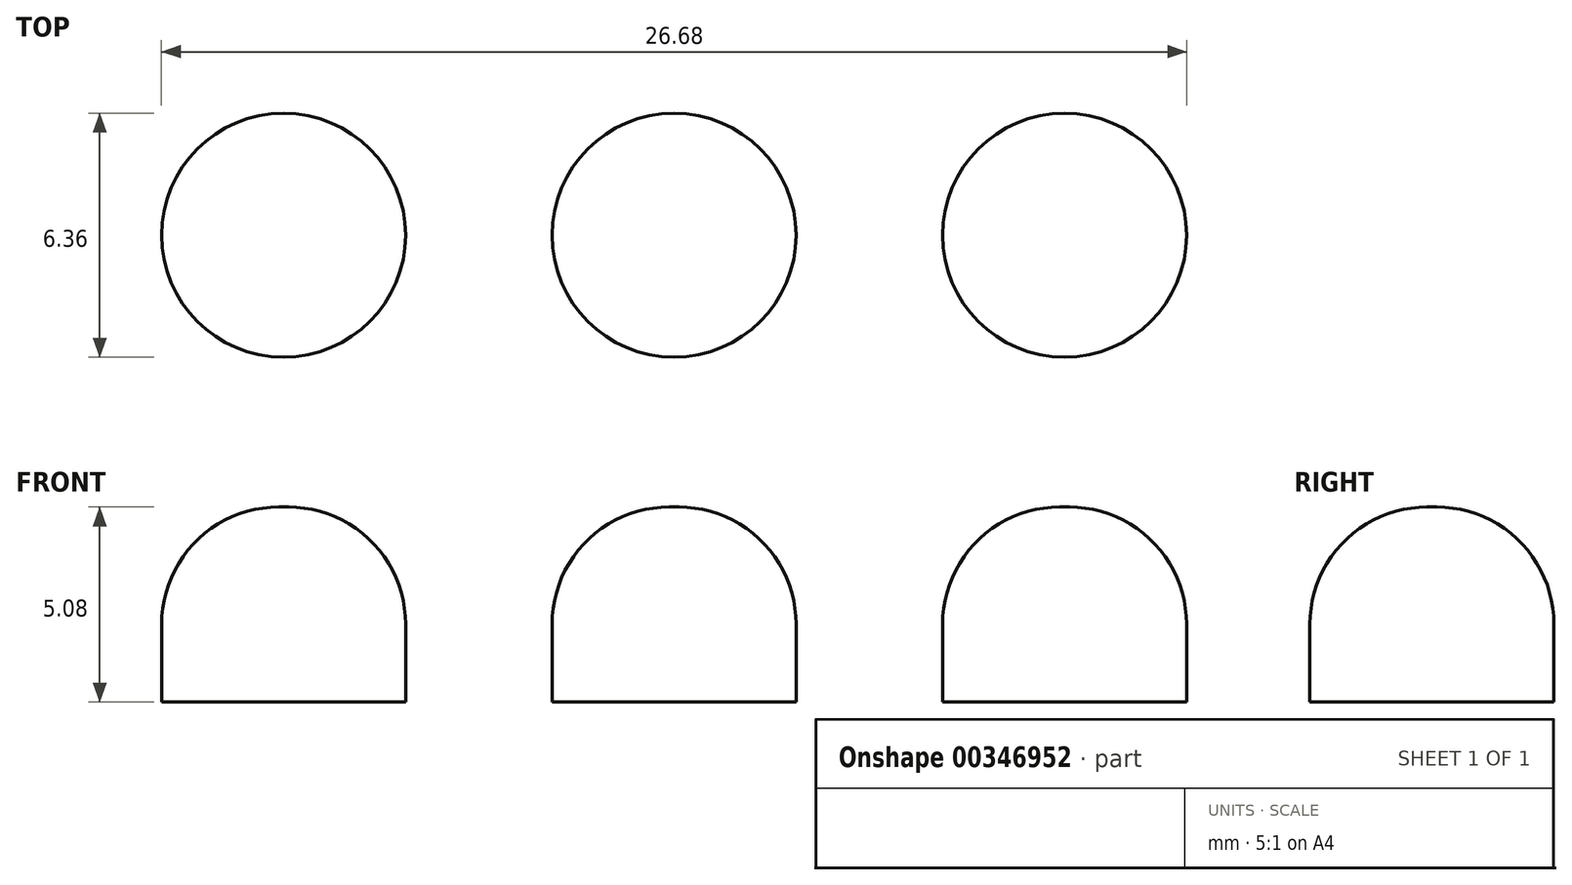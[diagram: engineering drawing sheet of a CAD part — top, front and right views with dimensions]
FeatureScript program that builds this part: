
annotation { "Feature Type Name" : "Feature", "Feature Type Description" : "" }
export const myFeature = defineFeature(function(context is Context, id is Id, definition is map)
    precondition{}
    {
        {
            var Q0;
            Q0=qCreatedBy(makeId("Top.planeOp"),FACE);
            var sketch = newSketch(context, id + "F0", { "sketchPlane" : qUnion([Q0])});
            skCircle(sketch, "E0", {"center": v(-10.16, 0) * mm, "radius": 3.18 * mm});
            skSolve(sketch);
        }
        {
            var Q0;
            Q0=qCreatedBy(makeId("Top.planeOp"),FACE);
            var sketch = newSketch(context, id + "F1", { "sketchPlane" : qUnion([Q0])});
            skCircle(sketch, "E1", {"center": v(0, 0) * mm, "radius": 3.18 * mm});
            skSolve(sketch);
        }
        {
            var Q0;
            Q0=qCreatedBy(makeId("Top.planeOp"),FACE);
            var sketch = newSketch(context, id + "F2", { "sketchPlane" : qUnion([Q0])});
            skCircle(sketch, "E2", {"center": v(10.16, 0) * mm, "radius": 3.18 * mm});
            skSolve(sketch);
        }
        {
            var Q0;
            Q0=makeQuery(id+"F0.imprint","IMPRINT",FACE,{"disambiguationData":[TD([[makeQuery(id+"F0.imprint","IMPRINT",EDGE,{"derivedFrom":sQuery(id+"F0.wireOp",EDGE,"E0")}),1.0]])]});
            extrude(context, id + "F3", {"entities" : qUnion([Q0]), "depth" : 5.08 * mm});
        }
        {
            var Q0;
            Q0=makeQuery(id+"F1.imprint","IMPRINT",FACE,{"disambiguationData":[TD([[makeQuery(id+"F1.imprint","IMPRINT",EDGE,{"derivedFrom":sQuery(id+"F1.wireOp",EDGE,"E1")}),1.0]])]});
            extrude(context, id + "F4", {"entities" : qUnion([Q0]), "depth" : 5.08 * mm});
        }
        {
            var Q0;
            Q0=makeQuery(id+"F2.imprint","IMPRINT",FACE,{"disambiguationData":[TD([[makeQuery(id+"F2.imprint","IMPRINT",EDGE,{"derivedFrom":sQuery(id+"F2.wireOp",EDGE,"E2")}),1.0]])]});
            extrude(context, id + "F5", {"entities" : qUnion([Q0]), "depth" : 5.08 * mm});
        }
        {
            var Q0;
            Q0=makeQuery(id+"F3.opExtrude","CAP_EDGE",EDGE,{"disambiguationData":[OSD([sQuery(id+"F0.wireOp",EDGE,"E0")])],"isStart":false});
            fillet(context, id + "F6", {"entities" : qUnion([Q0]), "radius" : 3.05 * mm, "tangentPropagation" : true, "allowEdgeOverflow" : false});
        }
        {
            var Q0;
            Q0=makeQuery(id+"F4.opExtrude","CAP_EDGE",EDGE,{"disambiguationData":[OSD([sQuery(id+"F1.wireOp",EDGE,"E1")])],"isStart":false});
            var Q1;
            Q1=makeQuery(id+"F5.opExtrude","CAP_EDGE",EDGE,{"disambiguationData":[OSD([sQuery(id+"F2.wireOp",EDGE,"E2")])],"isStart":false});
            fillet(context, id + "F7", {"entities" : qUnion([Q0, Q1]), "radius" : 3.05 * mm, "tangentPropagation" : true, "allowEdgeOverflow" : false});
        }
    });
